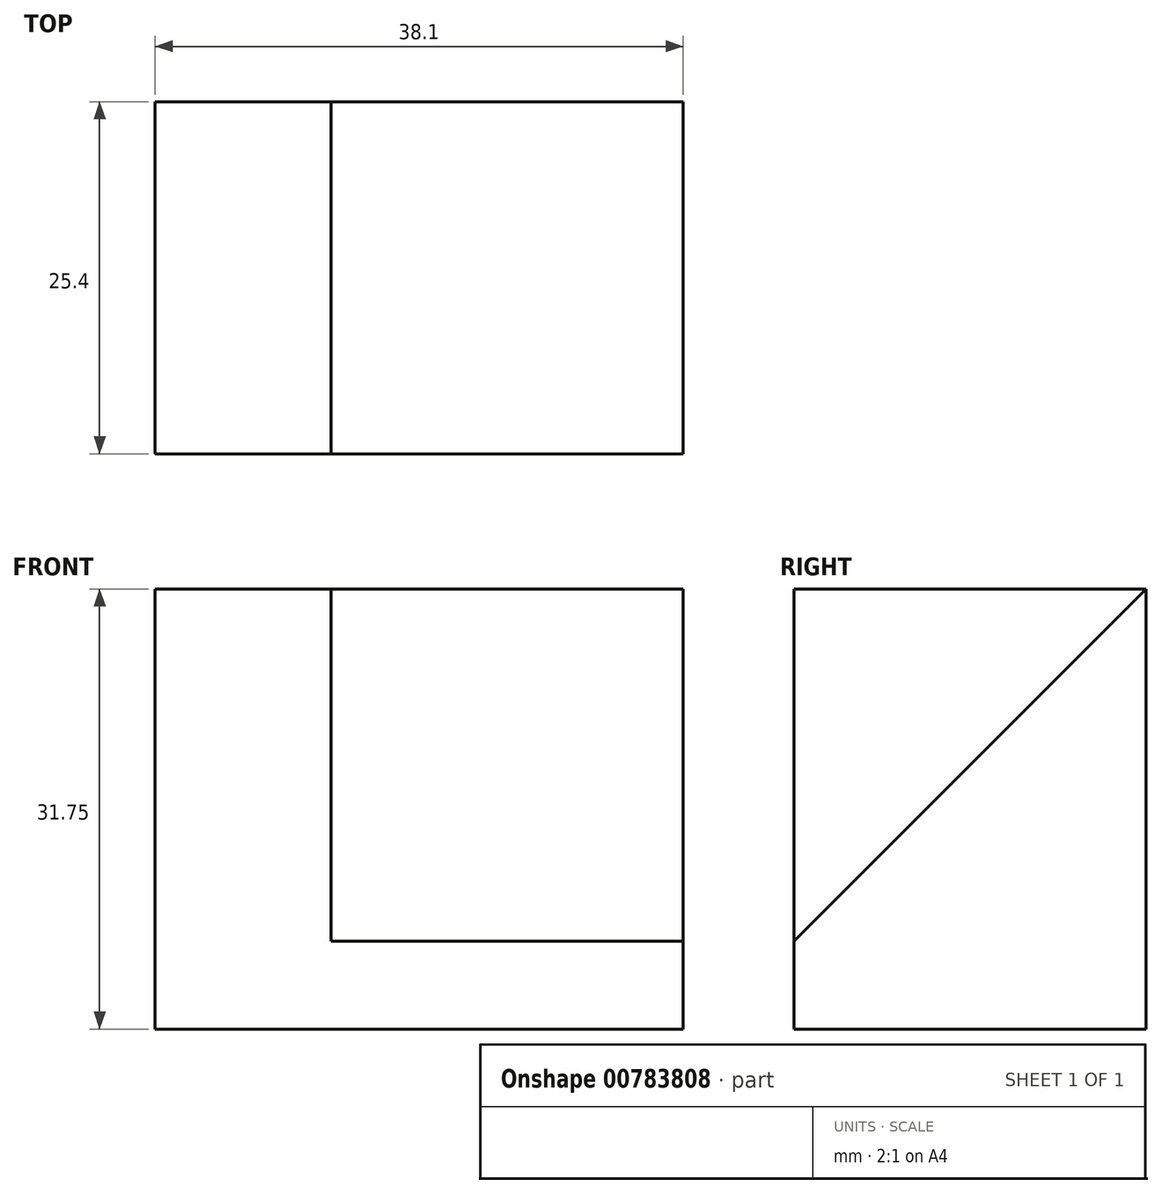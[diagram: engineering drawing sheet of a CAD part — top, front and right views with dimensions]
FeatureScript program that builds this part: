
annotation { "Feature Type Name" : "Feature", "Feature Type Description" : "" }
export const myFeature = defineFeature(function(context is Context, id is Id, definition is map)
    precondition{}
    {
        {
            var Q0;
            Q0=qCreatedBy(makeId("Front.planeOp"),FACE);
            var sketch = newSketch(context, id + "F0", { "sketchPlane" : qUnion([Q0])});
            skLineSegment(sketch, "E0", {"start": v(0, 0) * mm, "end": v(25.4, 0) * mm});
            skLineSegment(sketch, "E1", {"start": v(25.4, 0) * mm, "end": v(25.4, 31.75) * mm});
            skLineSegment(sketch, "E2", {"start": v(25.4, 31.75) * mm, "end": v(-12.7, 31.75) * mm});
            skLineSegment(sketch, "E3", {"start": v(-12.7, 31.75) * mm, "end": v(-12.7, 0) * mm});
            skLineSegment(sketch, "E4", {"start": v(-12.7, 0) * mm, "end": v(0, 0) * mm});
            skSolve(sketch);
        }
        {
            var Q0;
            Q0=makeQuery(id+"F0.imprint","IMPRINT",FACE,{"disambiguationData":[TD([[makeQuery(id+"F0.imprint","IMPRINT",EDGE,{"derivedFrom":sQuery(id+"F0.wireOp",EDGE,"E0")}),1.0]])]});
            extrude(context, id + "F1", {"entities" : qUnion([Q0]), "depth" : 25.4 * mm, "offsetDistance" : 25.4 * mm});
        }
        {
            var Q0;
            Q0=makeQuery(id+"F1.opExtrude","SWEPT_FACE",FACE,{"disambiguationData":[OSD([sQuery(id+"F0.wireOp",EDGE,"E1")])]});
            var sketch = newSketch(context, id + "F2", { "sketchPlane" : qUnion([Q0])});
            skLineSegment(sketch, "E5", {"start": v(-25.4, 0) * mm, "end": v(-25.4, 6.35) * mm});
            skLineSegment(sketch, "E6", {"start": v(0, 31.75) * mm, "end": v(-25.4, 6.35) * mm});
            skSolve(sketch);
        }
        {
            var Q0;
            {var subQ0=sQuery(id+"F2.wireOp",EDGE,"E6");Q0=makeQuery(id+"F2.imprint","IMPRINT",FACE,{"disambiguationData":[TD([[makeQuery(id+"F2.imprint","IMPRINT",EDGE,{"derivedFrom":subQ0}),-1.0]])]});}
            extrude(context, id + "F3", {"entities" : qUnion([Q0]), "operationType" : NewBodyOperationType.REMOVE, "oppositeDirection" : true, "depth" : 25.4 * mm, "offsetDistance" : 25.4 * mm});
        }
    });
